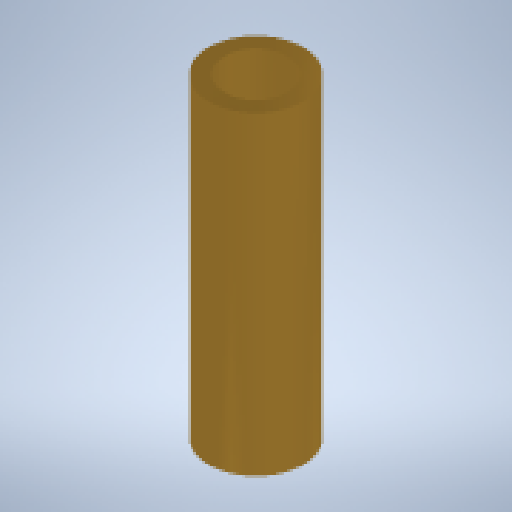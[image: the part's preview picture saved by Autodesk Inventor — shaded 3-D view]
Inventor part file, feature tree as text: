
AUTODESK INVENTOR PART (.ipt)
format: ipt  version: 2025 (Build 290162010, 162A)  size: 147,968 bytes
history: native  units: mm
features: extrude x1, sketch x1
ambient origin geometry x8: Origin, YZ Plane, XZ Plane, XY Plane, X Axis, Y Axis, Z Axis, Center Point
bodies: Volumenkörper1 (feature_tree)
feature tree (2):
  extrude  "Extrusion1"  Depth=20.0mm
  sketch  "Skizze1"  dims[d0=4.0mm d1=6.0mm d2=20.0mm d3=0.0mm]
